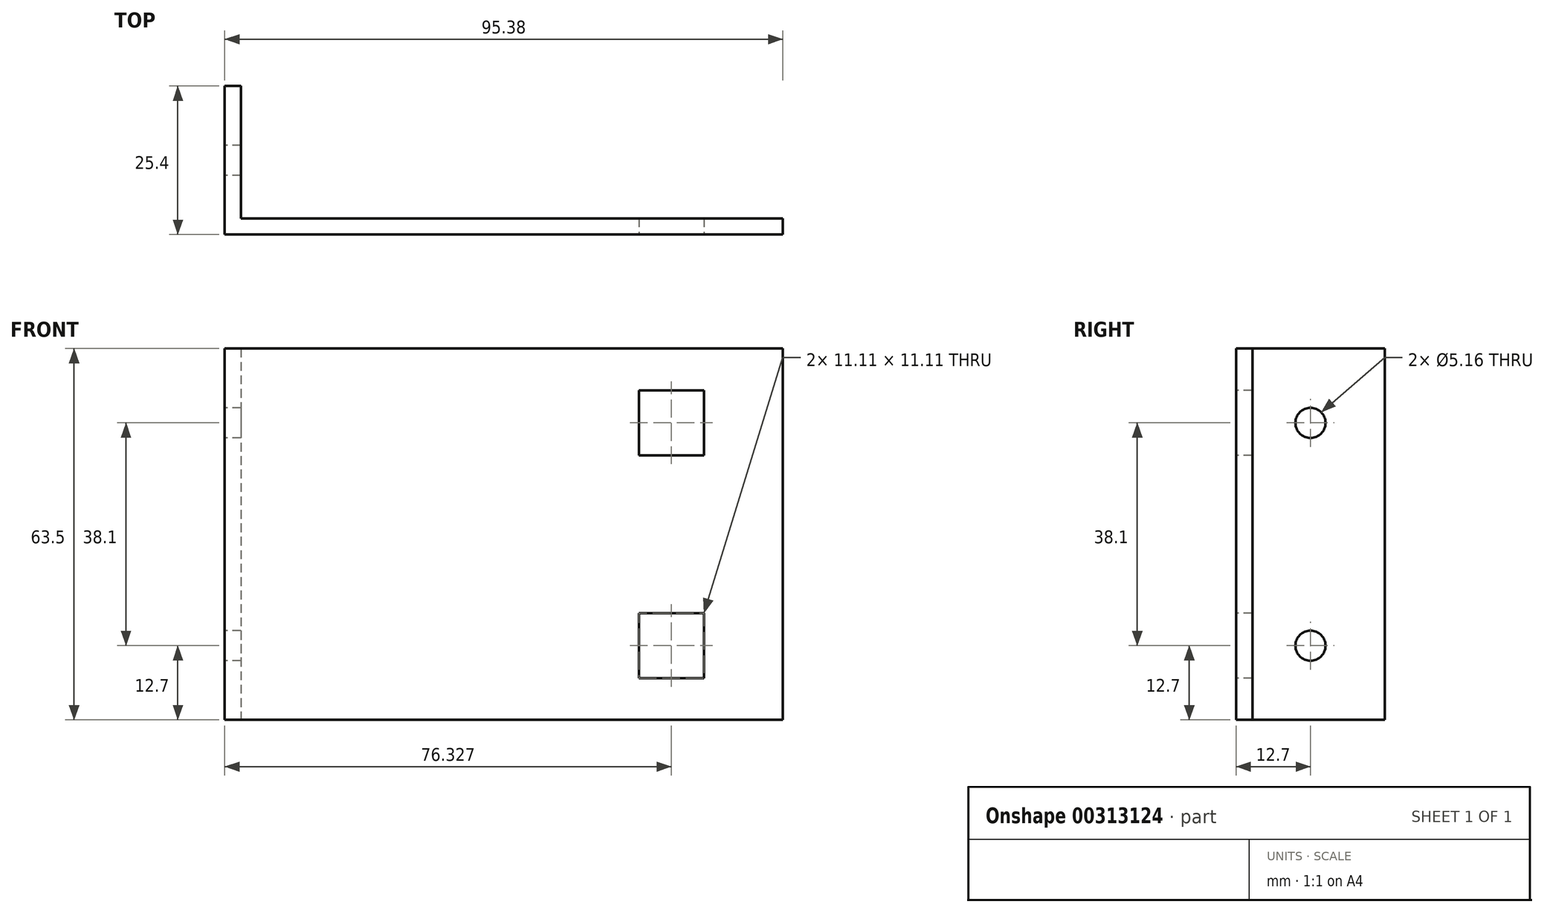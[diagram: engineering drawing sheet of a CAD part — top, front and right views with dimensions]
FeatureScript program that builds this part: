
annotation { "Feature Type Name" : "Feature", "Feature Type Description" : "" }
export const myFeature = defineFeature(function(context is Context, id is Id, definition is map)
    precondition{}
    {
        {
            var Q0;
            Q0=qCreatedBy(makeId("Top.planeOp"),FACE);
            var sketch = newSketch(context, id + "F0", { "sketchPlane" : qUnion([Q0])});
            skLineSegment(sketch, "E0.bottom", {"start": v(0, 0) * mm, "end": v(95.38, 0) * mm});
            skLineSegment(sketch, "E0.top", {"start": v(0, 25.4) * mm, "end": v(95.38, 25.4) * mm});
            skLineSegment(sketch, "E0.left", {"start": v(0, 0) * mm, "end": v(0, 25.4) * mm});
            skLineSegment(sketch, "E0.right", {"start": v(95.38, 0) * mm, "end": v(95.38, 25.4) * mm});
            skSolve(sketch);
        }
        {
            var Q0;
            Q0=qSketchRegion(id+"F0",true);
            extrude(context, id + "F1", {"entities" : qUnion([Q0]), "endBound" : BoundingType.SYMMETRIC, "depth" : 63.5 * mm});
        }
        {
            var Q0;
            Q0=makeQuery(id+"F1.opExtrude","SWEPT_FACE",FACE,{"disambiguationData":[OSD([sQuery(id+"F0.wireOp",EDGE,"E0.right")])]});
            var Q1;
            Q1=makeQuery(id+"F1.opExtrude","CAP_FACE",FACE,{"disambiguationData":[OSD([sQuery(id+"F0.wireOp",EDGE,"E0.bottom"),sQuery(id+"F0.wireOp",EDGE,"E0.top"),sQuery(id+"F0.wireOp",EDGE,"E0.left"),sQuery(id+"F0.wireOp",EDGE,"E0.right")])],"isStart":false});
            var Q2;
            Q2=makeQuery(id+"F1.opExtrude","CAP_FACE",FACE,{"disambiguationData":[OSD([sQuery(id+"F0.wireOp",EDGE,"E0.bottom"),sQuery(id+"F0.wireOp",EDGE,"E0.top"),sQuery(id+"F0.wireOp",EDGE,"E0.left"),sQuery(id+"F0.wireOp",EDGE,"E0.right")])],"isStart":true});
            var Q3;
            Q3=makeQuery(id+"F1.opExtrude","SWEPT_FACE",FACE,{"disambiguationData":[OSD([sQuery(id+"F0.wireOp",EDGE,"E0.top")])]});
            shell(context, id + "F2", {"entities" : qUnion([Q0, Q1, Q2, Q3]), "thickness" : 2.78 * mm});
        }
        {
            var Q0;
            Q0=makeQuery(id+"F1.opExtrude","SWEPT_FACE",FACE,{"disambiguationData":[OSD([sQuery(id+"F0.wireOp",EDGE,"E0.bottom")])]});
            var sketch = newSketch(context, id + "F3", { "sketchPlane" : qUnion([Q0])});
            skLineSegment(sketch, "E1.bottom", {"start": v(81.88, -13.5) * mm, "end": v(70.77, -13.5) * mm});
            skLineSegment(sketch, "E1.top", {"start": v(81.88, -24.6) * mm, "end": v(70.77, -24.6) * mm});
            skLineSegment(sketch, "E1.left", {"start": v(81.88, -13.5) * mm, "end": v(81.88, -24.6) * mm});
            skLineSegment(sketch, "E1.right", {"start": v(70.77, -13.5) * mm, "end": v(70.77, -24.6) * mm});
            skPoint(sketch, "E1.middle", {"position": v(76.33, -19.05) * mm});
            skPoint(sketch, "E1.middle.positionSnap0", {"position": v(47.69, -31.75) * mm});
            skPoint(sketch, "E1.centerSnap0", {"position": v(47.69, -31.75) * mm});
            skPoint(sketch, "E2.0.1.0", {"position": v(76.33, 19.05) * mm});
            skLineSegment(sketch, "E2.0.1.1", {"start": v(70.77, 24.6) * mm, "end": v(70.77, 13.5) * mm});
            skLineSegment(sketch, "E2.0.1.2", {"start": v(81.88, 24.6) * mm, "end": v(81.88, 13.5) * mm});
            skLineSegment(sketch, "E2.0.1.3", {"start": v(81.88, 13.5) * mm, "end": v(70.77, 13.5) * mm});
            skLineSegment(sketch, "E2.0.1.4", {"start": v(81.88, 24.6) * mm, "end": v(70.77, 24.6) * mm});
            skLineSegment(sketch, "E2.direction1", {"start": v(26.2, -24.6) * mm, "end": v(70.77, -24.6) * mm, "construction": true});
            skLineSegment(sketch, "E2.direction2", {"start": v(70.77, -24.6) * mm, "end": v(70.77, 13.5) * mm, "construction": true});
            skSolve(sketch);
        }
        {
            var Q0;
            Q0=qSketchRegion(id+"F3",true);
            extrude(context, id + "F4", {"entities" : qUnion([Q0]), "operationType" : NewBodyOperationType.REMOVE, "endBound" : BoundingType.THROUGH_ALL, "oppositeDirection" : true, "depth" : 25.4 * mm});
        }
        {
            var Q0;
            Q0=makeQuery(id+"F1.opExtrude","SWEPT_FACE",FACE,{"disambiguationData":[OSD([sQuery(id+"F0.wireOp",EDGE,"E0.left")])]});
            var sketch = newSketch(context, id + "F5", { "sketchPlane" : qUnion([Q0])});
            skCircle(sketch, "E3", {"center": v(-12.7, 19.05) * mm, "radius": 2.58 * mm});
            skPoint(sketch, "E3.centerSnap0", {"position": v(-12.7, 31.75) * mm});
            skCircle(sketch, "E4", {"center": v(-12.7, -19.05) * mm, "radius": 2.58 * mm});
            skLineSegment(sketch, "E5", {"start": v(-12.7, 19.05) * mm, "end": v(-12.7, -19.05) * mm, "construction": true});
            skPoint(sketch, "E6", {"position": v(-12.7, 0) * mm});
            skSolve(sketch);
        }
        {
            var Q0;
            Q0 = qSketchRegion(id + "F5", true);
            extrude(context, id + "F6", {"entities" : qUnion([Q0]), "operationType" : NewBodyOperationType.REMOVE, "endBound" : BoundingType.THROUGH_ALL, "oppositeDirection" : true, "depth" : 25.4 * mm});
        }
    });
